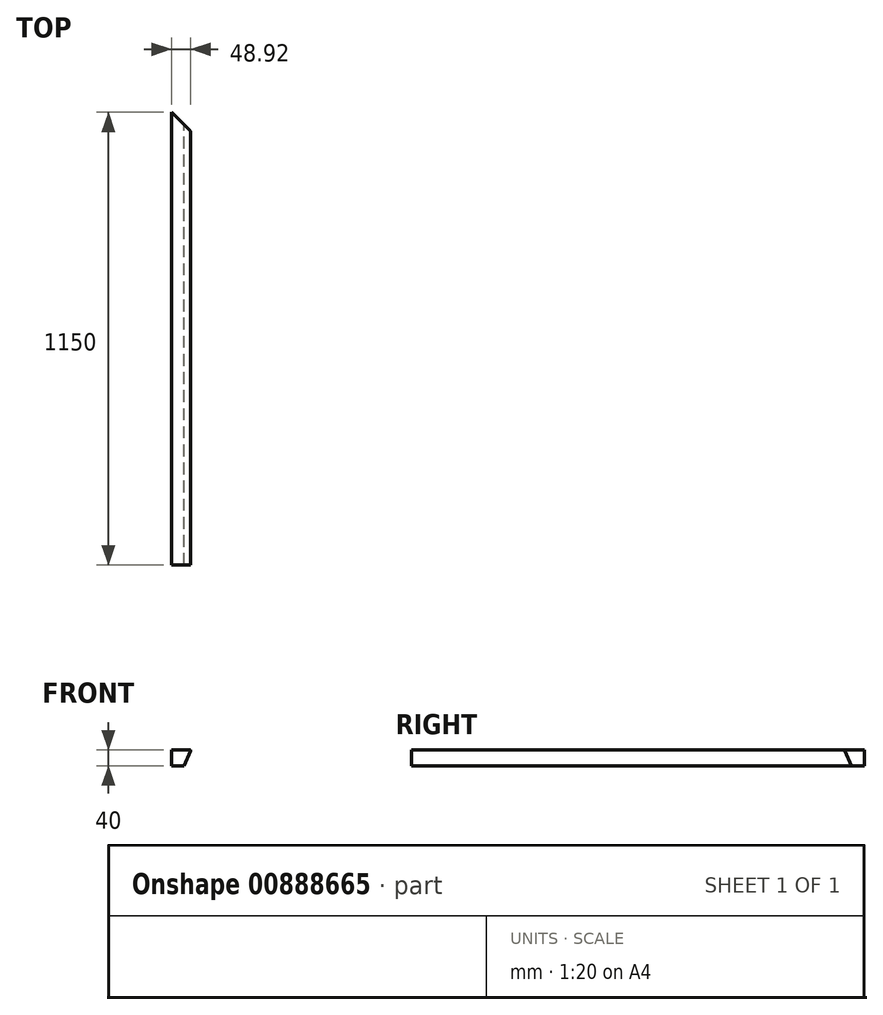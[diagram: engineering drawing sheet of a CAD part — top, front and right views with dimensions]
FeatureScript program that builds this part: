
annotation { "Feature Type Name" : "Feature", "Feature Type Description" : "" }
export const myFeature = defineFeature(function(context is Context, id is Id, definition is map)
    precondition{}
    {
        {
            var Q0;
            Q0=qCreatedBy(makeId("Front.planeOp"),FACE);
            var sketch = newSketch(context, id + "F0", { "sketchPlane" : qUnion([Q0])});
            skLineSegment(sketch, "E0.bottom", {"start": v(0, 0) * mm, "end": v(32.2, 0) * mm});
            skLineSegment(sketch, "E0.top", {"start": v(0, 40) * mm, "end": v(50, 40) * mm});
            skLineSegment(sketch, "E0.left", {"start": v(0, 0) * mm, "end": v(0, 40) * mm});
            skLineSegment(sketch, "E1", {"start": v(50, 40) * mm, "end": v(32.2, 0) * mm});
            skSolve(sketch);
        }
        {
            var Q0;
            Q0=qSketchRegion(id+"F0",true);
            extrude(context, id + "F1", {"entities" : qUnion([Q0]), "depth" : 1150 * mm, "offsetDistance" : 25 * mm});
        }
        {
            var Q0;
            Q0=makeQuery(id+"F1.opExtrude","SWEPT_EDGE",EDGE,{"disambiguationData":[OSD([sQuery(id+"F0.wireOp",EDGE,"E0.top"),sQuery(id+"F0.wireOp",EDGE,"E1")])]});
            fillet(context, id + "F2", {"entities" : qUnion([Q0]), "radius" : 2 * mm, "tangentPropagation" : true, "allowEdgeOverflow" : false});
        }
        {
            var Q0;
            Q0=makeQuery(id+"F1.opExtrude","SWEPT_FACE",FACE,{"disambiguationData":[OSD([sQuery(id+"F0.wireOp",EDGE,"E0.top")])]});
            var sketch = newSketch(context, id + "F3", { "sketchPlane" : qUnion([Q0])});
            skLineSegment(sketch, "E2", {"start": v(0, 0) * mm, "end": v(57.1, -57.1) * mm});
            skLineSegment(sketch, "E3", {"start": v(0, 0) * mm, "end": v(57, 0) * mm});
            skLineSegment(sketch, "E4", {"start": v(57, 0) * mm, "end": v(57.1, -57.1) * mm});
            skSolve(sketch);
        }
        {
            var Q0;
            {var subQ0=sQuery(id+"F3.wireOp",EDGE,"E4");Q0=makeQuery(id+"F3.imprint","IMPRINT",FACE,{"disambiguationData":[TD([[makeQuery(id+"F3.imprint","IMPRINT",EDGE,{"derivedFrom":subQ0}),-1.0]])]});}
            var Q1;
            {var subQ0=sQuery(id+"F3.wireOp",EDGE,"E3");var subQ1=sQuery(id+"F3.wireOp",EDGE,"E2");var subQ2=sQuery(id+"F0.wireOp",EDGE,"E0.top");var subQ3=makeQuery(id+"F3.imprint","INTERSECT",VERTEX,{"derivedFrom":[makeQuery(id+"F1.opExtrude","SWEPT_EDGE",EDGE,{"disambiguationData":[OSD([subQ2,sQuery(id+"F0.wireOp",EDGE,"E0.left")])]}),subQ1,subQ0]});Q1=makeQuery(id+"F3.imprint","IMPRINT",FACE,{"disambiguationData":[TD([[makeQuery(id+"F3.imprint","IMPRINT",EDGE,{"disambiguationData":[TD([[subQ3,-1.0]])],"derivedFrom":subQ1}),1.0]])]});}
            extrude(context, id + "F4", {"entities" : qUnion([Q0, Q1]), "operationType" : NewBodyOperationType.REMOVE, "endBound" : BoundingType.THROUGH_ALL, "oppositeDirection" : true, "depth" : 25 * mm, "offsetDistance" : 25 * mm});
        }
    });
